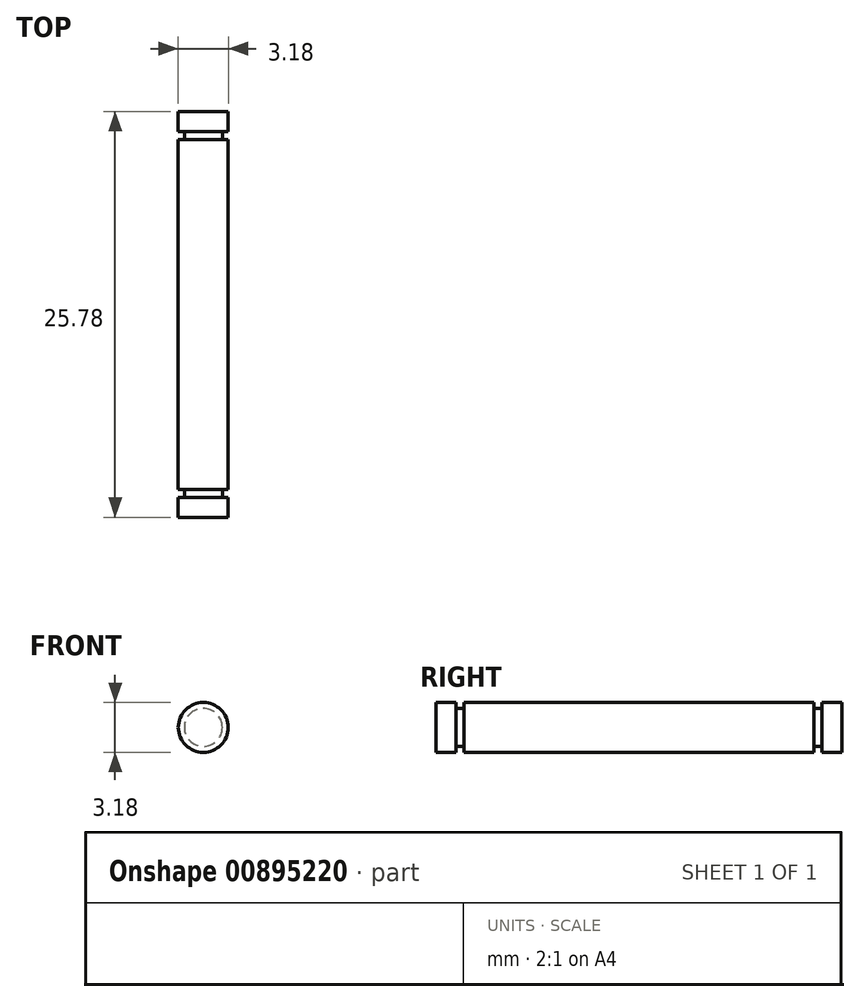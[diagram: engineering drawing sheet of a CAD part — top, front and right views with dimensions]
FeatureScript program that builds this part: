
annotation { "Feature Type Name" : "Feature", "Feature Type Description" : "" }
export const myFeature = defineFeature(function(context is Context, id is Id, definition is map)
    precondition{}
    {
        {
            var Q0;
            Q0=qCreatedBy(makeId("Front.planeOp"),FACE);
            var sketch = newSketch(context, id + "F0", { "sketchPlane" : qUnion([Q0])});
            skCircle(sketch, "E0", {"center": v(0, 0) * mm, "radius": 1.59 * mm});
            skSolve(sketch);
        }
        {
            var Q0;
            Q0 = qSketchRegion(id + "F0", true);
            extrude(context, id + "F1", {"entities" : qUnion([Q0]), "endBound" : BoundingType.SYMMETRIC, "depth" : 22.22 * mm, "offsetDistance" : 25.4 * mm});
        }
        {
            var Q0;
            Q0=makeQuery(id+"F1.opExtrude","CAP_FACE",FACE,{"disambiguationData":[OSD([sQuery(id+"F0.wireOp",EDGE,"E0")])],"isStart":false});
            var sketch = newSketch(context, id + "F2", { "sketchPlane" : qUnion([Q0])});
            skCircle(sketch, "E1", {"center": v(0, 0) * mm, "radius": 1.2 * mm});
            skSolve(sketch);
        }
        {
            var Q0;
            Q0=makeQuery(id+"F2.imprint","IMPRINT",FACE,{"disambiguationData":[TD([[makeQuery(id+"F2.imprint","IMPRINT",EDGE,{"derivedFrom":sQuery(id+"F2.wireOp",EDGE,"E1")}),1.0]])]});
            extrude(context, id + "F3", {"entities" : qUnion([Q0]), "operationType" : NewBodyOperationType.ADD, "depth" : 0.5 * mm, "offsetDistance" : 25.4 * mm});
        }
        {
            var Q0;
            Q0=makeQuery(id+"F3.opExtrude","CAP_FACE",FACE,{"disambiguationData":[OSD([sQuery(id+"F2.wireOp",EDGE,"E1")])],"isStart":false});
            var sketch = newSketch(context, id + "F4", { "sketchPlane" : qUnion([Q0])});
            skCircle(sketch, "E2", {"center": v(0, 0) * mm, "radius": 1.59 * mm});
            skSolve(sketch);
        }
        {
            var Q0;
            Q0=makeQuery(id+"F4.imprint","IMPRINT",FACE,{"disambiguationData":[TD([[makeQuery(id+"F4.imprint","IMPRINT",EDGE,{"derivedFrom":sQuery(id+"F4.wireOp",EDGE,"E2")}),1.0]])]});
            var Q1;
            Q1=makeQuery(id+"F4.imprint","IMPRINT",FACE,{"disambiguationData":[TD([[makeQuery(id+"F4.imprint","IMPRINT",EDGE,{"derivedFrom":makeQuery(id+"F3.opExtrude","CAP_EDGE",EDGE,{"disambiguationData":[OSD([sQuery(id+"F2.wireOp",EDGE,"E1")])],"isStart":false})}),1.0]])]});
            extrude(context, id + "F5", {"entities" : qUnion([Q0, Q1]), "operationType" : NewBodyOperationType.ADD, "depth" : 1.27 * mm, "offsetDistance" : 25.4 * mm});
        }
        {
            var Q0;
            Q0=makeQuery(id+"F1.opExtrude","CAP_FACE",FACE,{"disambiguationData":[OSD([sQuery(id+"F0.wireOp",EDGE,"E0")])],"isStart":true});
            var sketch = newSketch(context, id + "F6", { "sketchPlane" : qUnion([Q0])});
            skCircle(sketch, "E3", {"center": v(0, 0) * mm, "radius": 1.2 * mm});
            skSolve(sketch);
        }
        {
            var Q0;
            Q0=makeQuery(id+"F6.imprint","IMPRINT",FACE,{"disambiguationData":[TD([[makeQuery(id+"F6.imprint","IMPRINT",EDGE,{"derivedFrom":sQuery(id+"F6.wireOp",EDGE,"E3")}),1.0]])]});
            extrude(context, id + "F7", {"entities" : qUnion([Q0]), "operationType" : NewBodyOperationType.ADD, "depth" : 0.5 * mm, "offsetDistance" : 25.4 * mm});
        }
        {
            var Q0;
            Q0=makeQuery(id+"F7.opExtrude","CAP_FACE",FACE,{"disambiguationData":[OSD([sQuery(id+"F6.wireOp",EDGE,"E3")])],"isStart":false});
            var sketch = newSketch(context, id + "F8", { "sketchPlane" : qUnion([Q0])});
            skCircle(sketch, "E4", {"center": v(0, 0) * mm, "radius": 1.59 * mm});
            skSolve(sketch);
        }
        {
            var Q0;
            Q0=makeQuery(id+"F8.imprint","IMPRINT",FACE,{"disambiguationData":[TD([[makeQuery(id+"F8.imprint","IMPRINT",EDGE,{"derivedFrom":sQuery(id+"F8.wireOp",EDGE,"E4")}),1.0]])]});
            var Q1;
            Q1=makeQuery(id+"F8.imprint","IMPRINT",FACE,{"disambiguationData":[TD([[makeQuery(id+"F8.imprint","IMPRINT",EDGE,{"derivedFrom":makeQuery(id+"F7.opExtrude","CAP_EDGE",EDGE,{"disambiguationData":[OSD([sQuery(id+"F6.wireOp",EDGE,"E3")])],"isStart":false})}),1.0]])]});
            extrude(context, id + "F9", {"entities" : qUnion([Q0, Q1]), "operationType" : NewBodyOperationType.ADD, "depth" : 1.27 * mm, "offsetDistance" : 25.4 * mm});
        }
    });
